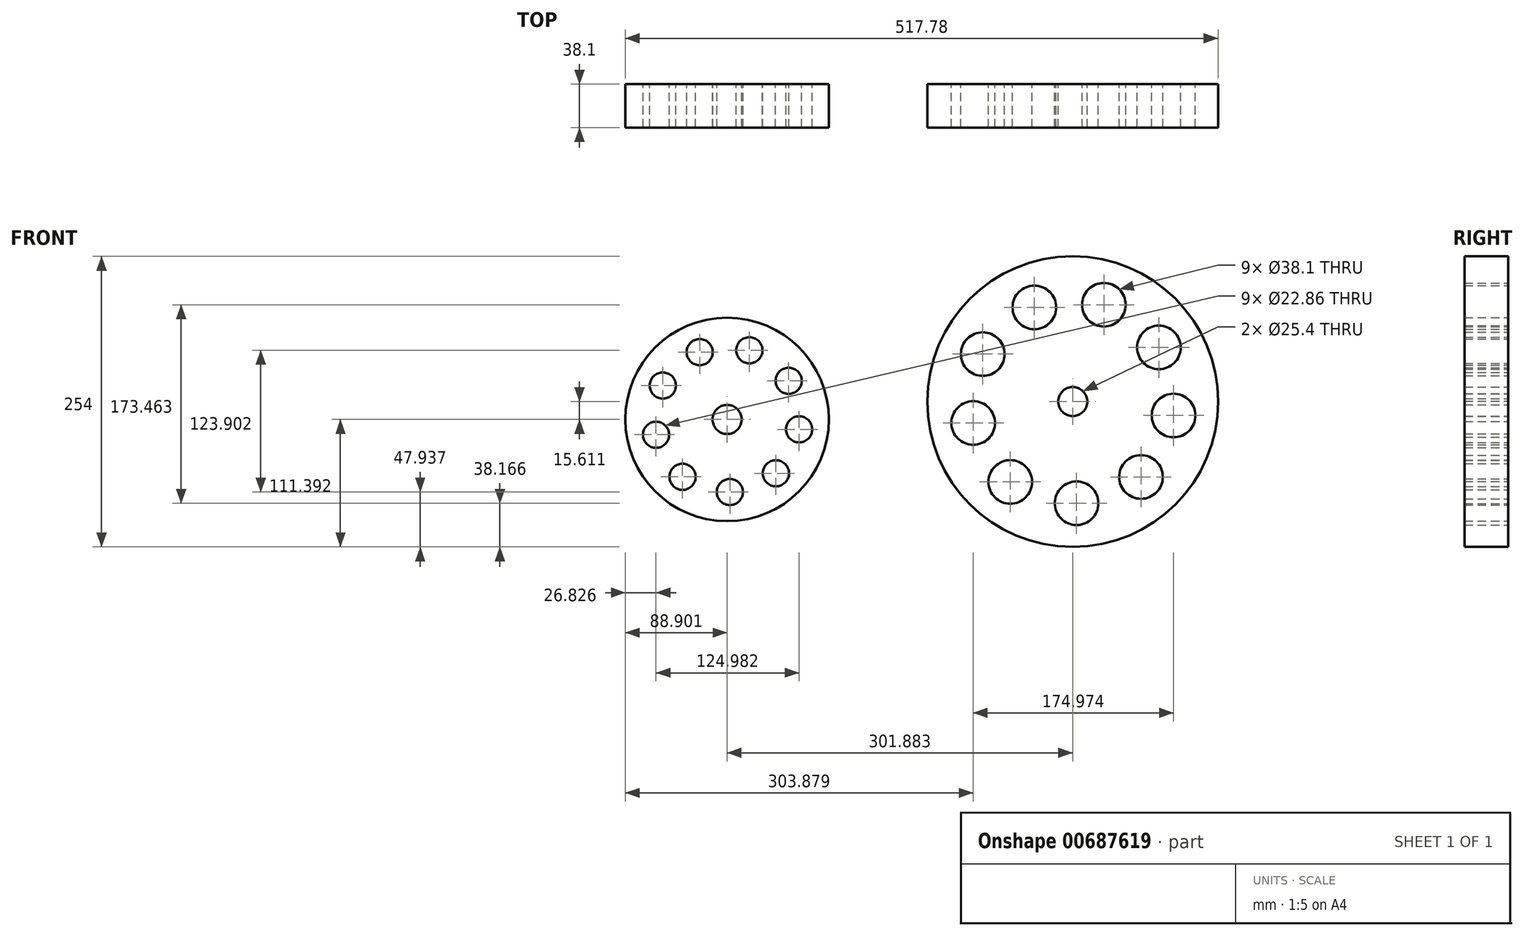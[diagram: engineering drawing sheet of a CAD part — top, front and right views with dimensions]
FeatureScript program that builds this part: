
annotation { "Feature Type Name" : "Feature", "Feature Type Description" : "" }
export const myFeature = defineFeature(function(context is Context, id is Id, definition is map)
    precondition{}
    {
        {
            var Q0;
            Q0=qCreatedBy(makeId("Front.planeOp"),FACE);
            var sketch = newSketch(context, id + "F0", { "sketchPlane" : qUnion([Q0])});
            skCircle(sketch, "E0", {"center": v(-27.28, -9.6) * mm, "radius": 127 * mm});
            skCircle(sketch, "E1", {"center": v(-27.28, -9.6) * mm, "radius": 12.7 * mm});
            skCircle(sketch, "E2", {"center": v(-105.89, 31.92) * mm, "radius": 19.05 * mm});
            skCircle(sketch, "E3.1.0", {"center": v(-60.81, 72.74) * mm, "radius": 19.05 * mm});
            skCircle(sketch, "E3.2.0", {"center": v(-0.04, 75.03) * mm, "radius": 19.05 * mm});
            skCircle(sketch, "E3.3.0", {"center": v(47.98, 37.73) * mm, "radius": 19.05 * mm});
            skCircle(sketch, "E3.4.0", {"center": v(60.8, -21.72) * mm, "radius": 19.05 * mm});
            skCircle(sketch, "E3.5.0", {"center": v(32.4, -75.5) * mm, "radius": 19.05 * mm});
            skCircle(sketch, "E3.6.0", {"center": v(-23.92, -98.43) * mm, "radius": 19.05 * mm});
            skCircle(sketch, "E3.7.0", {"center": v(-81.81, -79.8) * mm, "radius": 19.05 * mm});
            skCircle(sketch, "E3.8.0", {"center": v(-114.18, -28.33) * mm, "radius": 19.05 * mm});
            skLineSegment(sketch, "E3.anchor1", {"start": v(-27.28, -9.6) * mm, "end": v(-105.89, 31.92) * mm, "construction": true});
            skLineSegment(sketch, "E3.anchor2", {"start": v(-27.28, -9.6) * mm, "end": v(-114.18, -28.33) * mm, "construction": true});
            skCircle(sketch, "E4", {"center": v(-329.16, -25.2) * mm, "radius": 88.9 * mm});
            skCircle(sketch, "E5", {"center": v(-329.16, -25.2) * mm, "radius": 12.7 * mm});
            skCircle(sketch, "E6", {"center": v(-385.31, 4.44) * mm, "radius": 11.43 * mm});
            skCircle(sketch, "E7.1.0", {"center": v(-353.11, 33.6) * mm, "radius": 11.43 * mm});
            skCircle(sketch, "E7.2.0", {"center": v(-309.7, 35.24) * mm, "radius": 11.43 * mm});
            skCircle(sketch, "E7.3.0", {"center": v(-275.4, 8.6) * mm, "radius": 11.43 * mm});
            skCircle(sketch, "E7.4.0", {"center": v(-266.25, -33.87) * mm, "radius": 11.43 * mm});
            skCircle(sketch, "E7.5.0", {"center": v(-286.54, -72.28) * mm, "radius": 11.43 * mm});
            skCircle(sketch, "E7.6.0", {"center": v(-326.76, -88.66) * mm, "radius": 11.43 * mm});
            skCircle(sketch, "E7.7.0", {"center": v(-368.11, -75.36) * mm, "radius": 11.43 * mm});
            skCircle(sketch, "E7.8.0", {"center": v(-391.23, -38.59) * mm, "radius": 11.43 * mm});
            skLineSegment(sketch, "E7.anchor1", {"start": v(-329.16, -25.2) * mm, "end": v(-385.31, 4.44) * mm, "construction": true});
            skLineSegment(sketch, "E7.anchor2", {"start": v(-329.16, -25.2) * mm, "end": v(-391.23, -38.59) * mm, "construction": true});
            skSolve(sketch);
        }
        {
            var Q0;
            Q0 = qSketchRegion(id + "F0", true);
            extrude(context, id + "F1", {"entities" : qUnion([Q0]), "depth" : 38.1 * mm, "offsetDistance" : 25.4 * mm});
        }
    });
